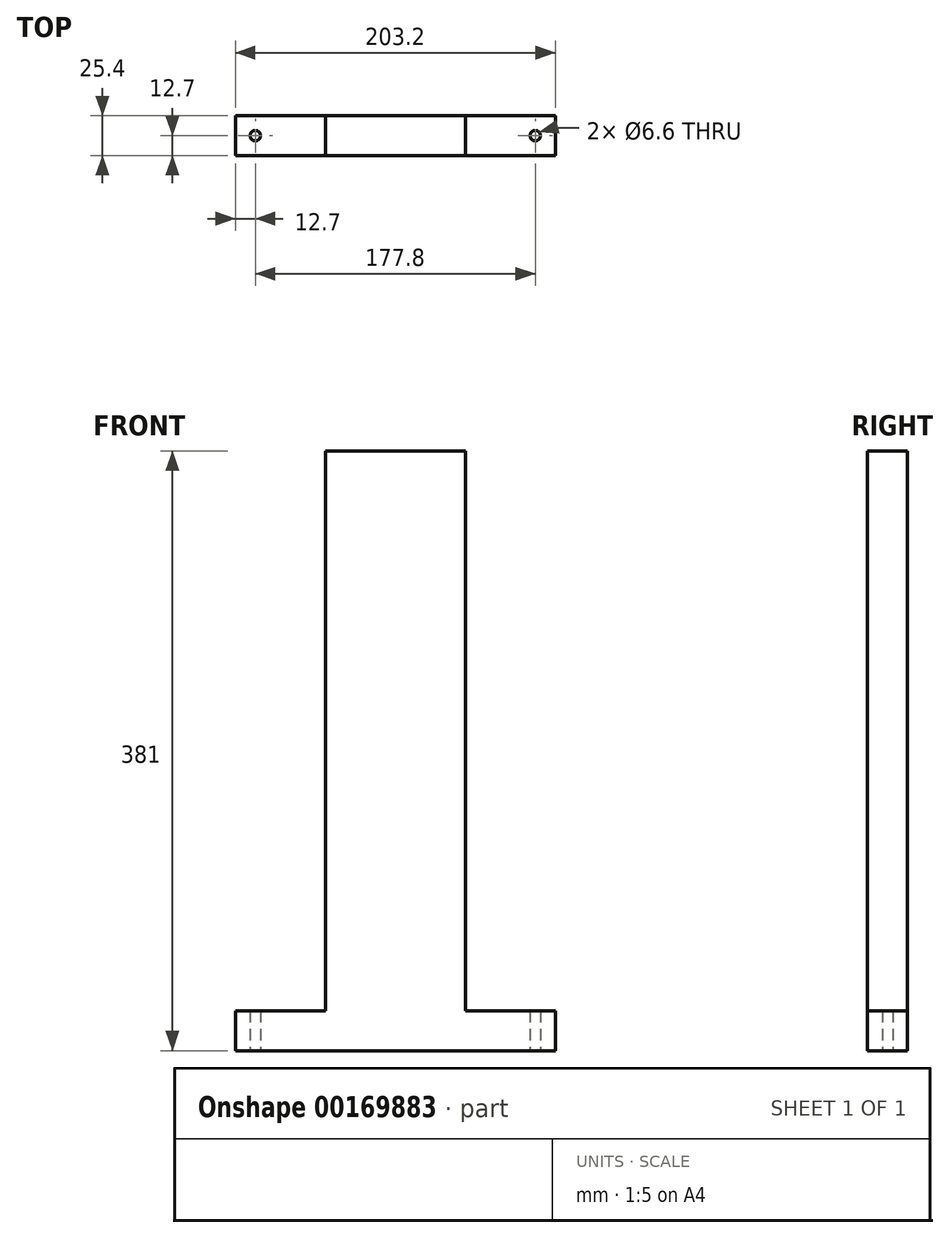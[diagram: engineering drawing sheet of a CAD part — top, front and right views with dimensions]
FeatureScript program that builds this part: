
annotation { "Feature Type Name" : "Feature", "Feature Type Description" : "" }
export const myFeature = defineFeature(function(context is Context, id is Id, definition is map)
    precondition{}
    {
        {
            var Q0;
            Q0=qCreatedBy(makeId("Top.planeOp"),FACE);
            var sketch = newSketch(context, id + "F0", { "sketchPlane" : qUnion([Q0])});
            skLineSegment(sketch, "E0.bottom", {"start": v(-101.6, -12.7) * mm, "end": v(101.6, -12.7) * mm});
            skLineSegment(sketch, "E0.top", {"start": v(-101.6, 12.7) * mm, "end": v(101.6, 12.7) * mm});
            skLineSegment(sketch, "E0.left", {"start": v(-101.6, -12.7) * mm, "end": v(-101.6, 12.7) * mm});
            skLineSegment(sketch, "E0.right", {"start": v(101.6, -12.7) * mm, "end": v(101.6, 12.7) * mm});
            skPoint(sketch, "E0.middle", {"position": v(0, 0) * mm});
            skLineSegment(sketch, "E1", {"start": v(-101.6, 0) * mm, "end": v(0, 0) * mm, "construction": true});
            skLineSegment(sketch, "E2", {"start": v(0, 12.7) * mm, "end": v(0, 0) * mm, "construction": true});
            skCircle(sketch, "E3", {"center": v(-88.9, 0) * mm, "radius": 3.3 * mm});
            skCircle(sketch, "E4.MirrorC", {"center": v(88.9, 0) * mm, "radius": 3.3 * mm});
            skSolve(sketch);
        }
        {
            var Q0;
            Q0=makeQuery(id+"F0.imprint","IMPRINT",FACE,{"disambiguationData":[TD([[makeQuery(id+"F0.imprint","IMPRINT",EDGE,{"derivedFrom":sQuery(id+"F0.wireOp",EDGE,"E0.bottom")}),1.0]])]});
            extrude(context, id + "F1", {"entities" : qUnion([Q0]), "depth" : 25.4 * mm});
        }
        {
            var Q0;
            Q0=makeQuery(id+"F1.opExtrude","CAP_FACE",FACE,{"disambiguationData":[OSD([sQuery(id+"F0.wireOp",EDGE,"E0.bottom"),sQuery(id+"F0.wireOp",EDGE,"E0.top"),sQuery(id+"F0.wireOp",EDGE,"E0.left"),sQuery(id+"F0.wireOp",EDGE,"E0.right"),sQuery(id+"F0.wireOp",EDGE,"E3"),sQuery(id+"F0.wireOp",EDGE,"E4.MirrorC")])],"isStart":false});
            var sketch = newSketch(context, id + "F2", { "sketchPlane" : qUnion([Q0])});
            skLineSegment(sketch, "E5.bottom", {"start": v(44.45, -12.7) * mm, "end": v(-44.45, -12.7) * mm});
            skLineSegment(sketch, "E5.top", {"start": v(44.45, 12.7) * mm, "end": v(-44.45, 12.7) * mm});
            skLineSegment(sketch, "E5.left", {"start": v(44.45, 12.7) * mm, "end": v(44.45, -12.7) * mm});
            skLineSegment(sketch, "E5.right", {"start": v(-44.45, 12.7) * mm, "end": v(-44.45, -12.7) * mm});
            skPoint(sketch, "E5.middle", {"position": v(0, 0) * mm});
            skSolve(sketch);
        }
        {
            var Q0;
            Q0=makeQuery(id+"F2.imprint","IMPRINT",FACE,{"disambiguationData":[TD([[makeQuery(id+"F2.imprint","IMPRINT",EDGE,{"derivedFrom":sQuery(id+"F2.wireOp",EDGE,"E5.bottom")}),-1.0]])]});
            var Q1;
            Q1=makeQuery(id+"F2.imprint","IMPRINT",FACE,{"disambiguationData":[TD([[makeQuery(id+"F2.imprint","IMPRINT",EDGE,{"derivedFrom":sQuery(id+"F2.wireOp",EDGE,"E5.bottom")}),1.0]])]});
            extrude(context, id + "F3", {"entities" : qUnion([Q0, Q1]), "operationType" : NewBodyOperationType.ADD, "depth" : 355.6 * mm});
        }
    });
